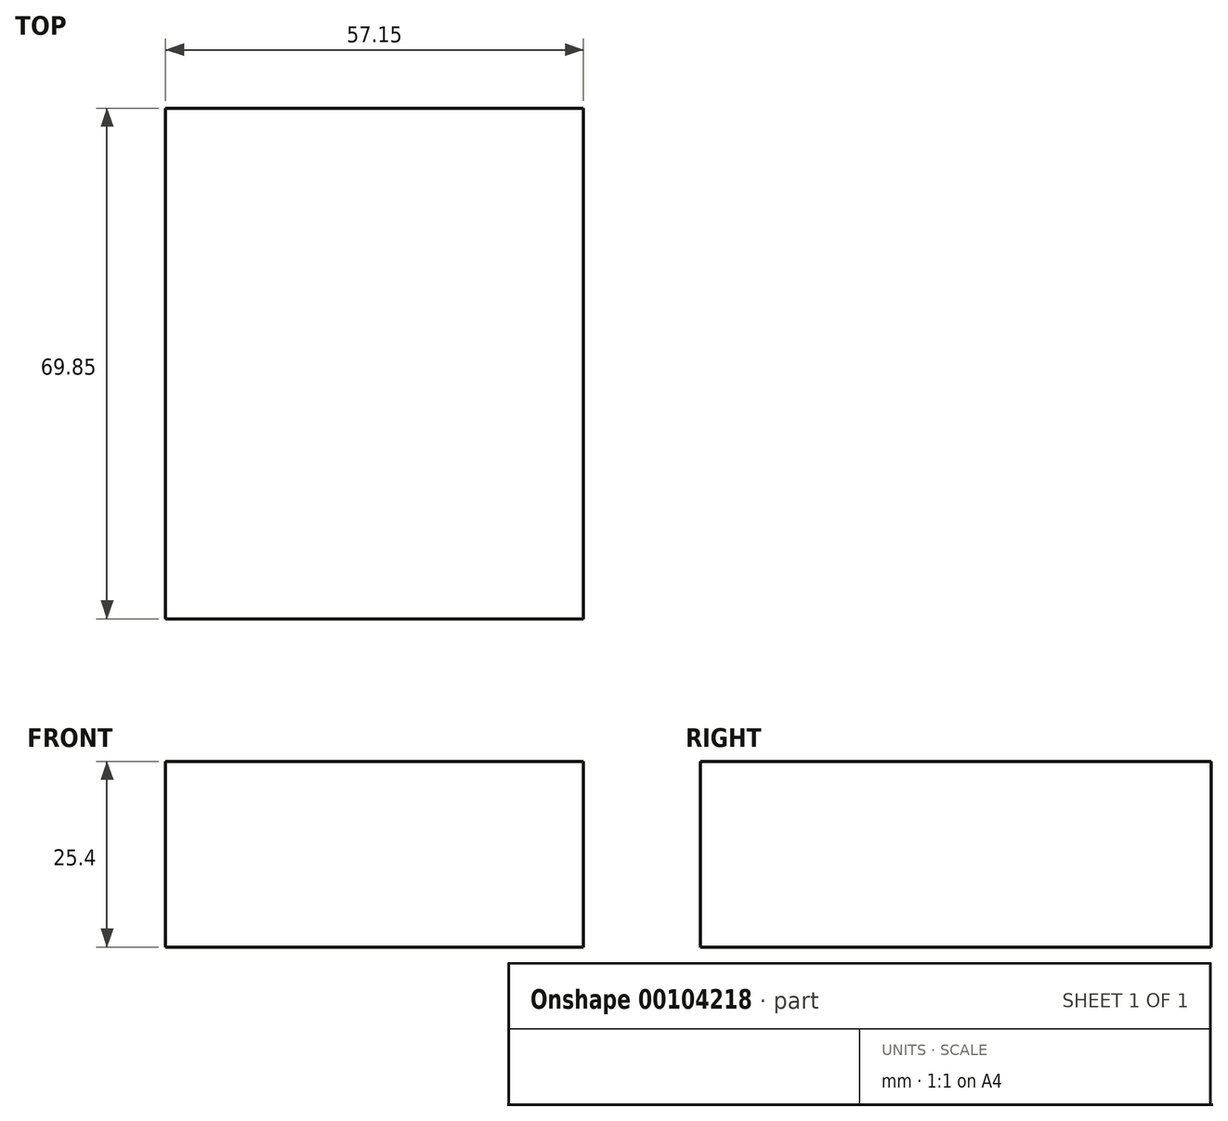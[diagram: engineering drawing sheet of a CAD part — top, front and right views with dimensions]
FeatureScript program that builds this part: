
annotation { "Feature Type Name" : "Feature", "Feature Type Description" : "" }
export const myFeature = defineFeature(function(context is Context, id is Id, definition is map)
    precondition{}
    {
        {
            var Q0;
            Q0=qCreatedBy(makeId("Top.planeOp"),FACE);
            var sketch = newSketch(context, id + "F0", { "sketchPlane" : qUnion([Q0])});
            skLineSegment(sketch, "E0.bottom", {"start": v(-33.37, 33.7) * mm, "end": v(23.78, 33.7) * mm});
            skLineSegment(sketch, "E0.top", {"start": v(-33.37, -36.15) * mm, "end": v(23.78, -36.15) * mm});
            skLineSegment(sketch, "E0.left", {"start": v(-33.37, 33.7) * mm, "end": v(-33.37, -36.15) * mm});
            skLineSegment(sketch, "E0.right", {"start": v(23.78, 33.7) * mm, "end": v(23.78, -36.15) * mm});
            skSolve(sketch);
        }
        {
            var Q0;
            Q0=makeQuery(id+"F0.imprint","IMPRINT",FACE,{"disambiguationData":[TD([[makeQuery(id+"F0.imprint","IMPRINT",EDGE,{"derivedFrom":sQuery(id+"F0.wireOp",EDGE,"E0.bottom")}),-1.0]])]});
            extrude(context, id + "F1", {"entities" : qUnion([Q0]), "depth" : 25.4 * mm});
        }
    });
